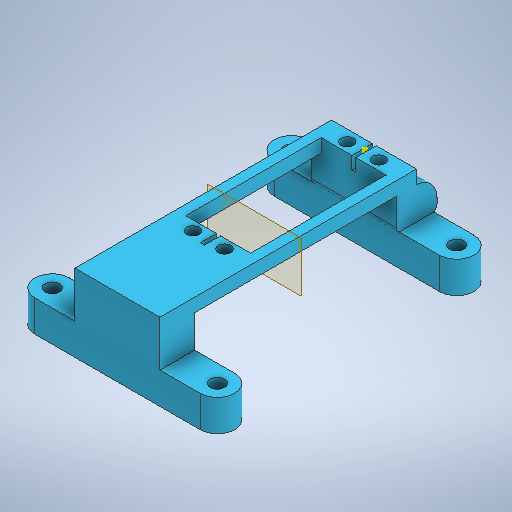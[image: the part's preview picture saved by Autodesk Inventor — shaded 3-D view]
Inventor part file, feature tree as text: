
AUTODESK INVENTOR PART (.ipt)
format: ipt  version: 2025.1 (Build 291241000, 241)  size: 390,656 bytes
history: native  units: in
note: dims shown in document units (in); Inventor stores cm internally (conversion verified against a paired STEP export)
features: sketch x8, extrude x7, fillet x2, other x2, plane x1, mirror x1
ambient origin geometry x8: Origin, YZ Plane, XZ Plane, XY Plane, X Axis, Y Axis, Z Axis, Center Point
bodies: Solid1 (feature_tree)
feature tree (21):
  extrude  "Extrusion1"  Depth=0.3937in TaperAngle=0.0deg
  extrude  "Extrusion2"  Depth=0.5118in
  fillet  "Fillet1"  Radius=0.5732in
  extrude  "Extrusion3"  Depth=0.0787in
  extrude  "Extrusion4"  Depth=0.3937in TaperAngle=0.0deg
  fillet  "Fillet2"  Radius=0.1688in
  extrude  "Extrusion5"  Depth=0.126in
  extrude  "Extrusion6"  Depth=0.126in
  plane  "Work Plane1"
  sketch  "Sketch7"  dims[d22=2.5197in d23=1.811in]
  mirror  "Mirror1"
  extrude  "Extrusion7"  Depth=2.5197in
  sketch  "Sketch1"  dims[d0=0.4331in d1=0.4331in d2=0.3937in d3=0.0in]
  sketch  "Sketch2"  dims[d4=1.063in d5=0.5118in d6=0.5732in d7=0.0in]
  sketch  "Sketch3"  dims[d8=0.0787in d12=0.3346in]
  sketch  "Sketch4"  dims[d13=0.3346in d14=0.3937in d15=0.0in d16=0.1688in d17=0.0in]
  sketch  "Sketch5"  dims[d18=0.2662in d19=0.126in]
  sketch  "Sketch6"  dims[d20=2.5197in d21=0.126in]
  sketch  "Sketch8"  dims[d24=0.3346in d25=0.1575in d26=0.3346in d27=0.1575in d28=0.2362in d29=0.2362in d30=0.0512in d32=0.1688in d33=0.0in d34=0.4331in d35=0.1688in d36=0.0in d37=-1.7126in d38=0.0472in d39=0.1575in d40=0.0in d41=0.1811in d42=0.1811in d43=0.0787in d44=0.0787in d9=0.0344in d10=0.0in d11=0.0in]
  other  "Finish1"
  other  "Finish2"
